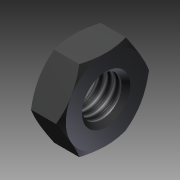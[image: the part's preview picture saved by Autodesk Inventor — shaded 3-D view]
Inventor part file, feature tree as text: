
AUTODESK INVENTOR PART (.ipt)
format: ipt  version: 2011 SP1 (Build 150282100, 282)  size: 122,880 bytes
history: native  units: mm
features: other x7, sketch x3, revolve x2, thread x1, extrude x1
ambient origin geometry x8: Origin, YZ Plane, XZ Plane, XY Plane, X Axis, Y Axis, Z Axis, Center Point
bodies: Solid1 (feature_tree)
feature tree (14):
  revolve  "Revolution1"  Angle=360.0deg
  revolve  "Revolution2"  [1 undecoded]
  thread  "Thread1"  [1 undecoded]
  extrude  "Extrusion1"  [1 undecoded]
  other  "DADO1_XY"
  other  "DADO1_YZ"
  other  "DADO1_ZX"
  other  "DADO1_X"
  other  "DADO1_Y"
  other  "DADO1_Z"
  other  "DADO1_Center"
  sketch  "Skizze_1"  dims[d0=360.0deg d1=360.0deg]
  sketch  "Skizze_2_ALT_Drilling_1"  dims[d2=2.917mm d3=0.0mm d4=4.0mm d5=0.0mm d6=0.0mm]
  sketch  "Skizze_3"
note: 3 required parameter values undecoded (feature->parameter linkage not recoverable at this tier; creation-order binding heuristic only, values carry confidence <= 0.55)